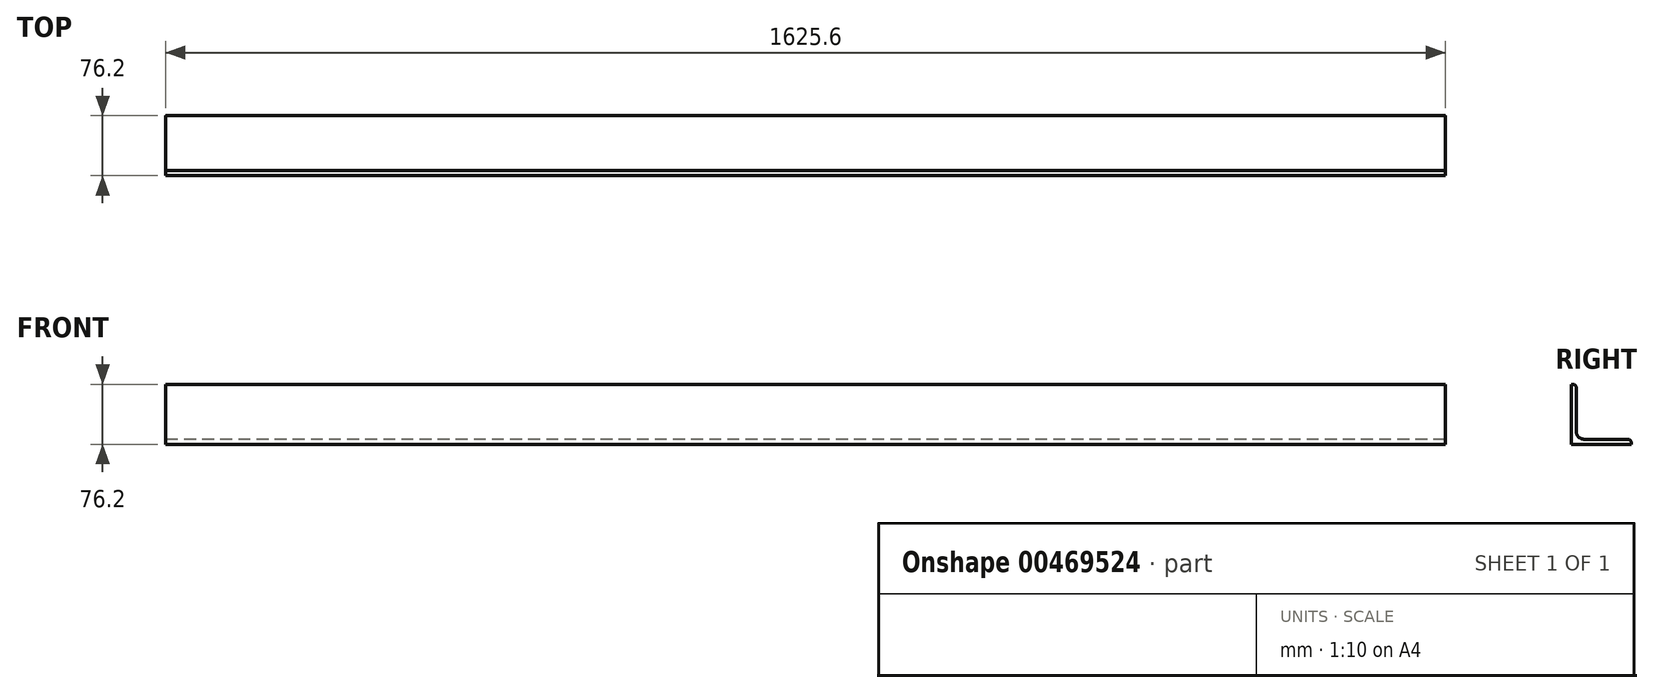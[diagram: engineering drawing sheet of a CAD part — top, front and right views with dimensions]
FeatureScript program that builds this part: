
annotation { "Feature Type Name" : "Feature", "Feature Type Description" : "" }
export const myFeature = defineFeature(function(context is Context, id is Id, definition is map)
    precondition{}
    {
        {
            var Q0;
            Q0=qCreatedBy(makeId("Right.planeOp"),FACE);
            var sketch = newSketch(context, id + "F0", { "sketchPlane" : qUnion([Q0])});
            skLineSegment(sketch, "E0", {"start": v(0, 76.2) * mm, "end": v(0, 0) * mm});
            skLineSegment(sketch, "E1", {"start": v(0, 0) * mm, "end": v(76.2, 0) * mm});
            skLineSegment(sketch, "E2", {"start": v(76.2, 0) * mm, "end": v(76.2, 1.59) * mm});
            skLineSegment(sketch, "E3", {"start": v(71.44, 6.35) * mm, "end": v(15.88, 6.35) * mm});
            skLineSegment(sketch, "E4", {"start": v(6.35, 15.87) * mm, "end": v(6.35, 71.44) * mm});
            skLineSegment(sketch, "E5", {"start": v(1.59, 76.2) * mm, "end": v(0, 76.2) * mm});
            skPoint(sketch, "E6.visualSharp", {"position": v(6.35, 76.2) * mm});
            skArc(sketch, "E6.filletArc", {"start": v(6.35, 71.44) * mm, "mid": v(4.96, 74.8) * mm, "end": v(1.59, 76.2) * mm});
            skPoint(sketch, "E7.visualSharp", {"position": v(76.2, 6.35) * mm});
            skArc(sketch, "E7.filletArc", {"start": v(76.2, 1.59) * mm, "mid": v(74.8, 4.96) * mm, "end": v(71.44, 6.35) * mm});
            skPoint(sketch, "E8.visualSharp", {"position": v(6.35, 6.35) * mm});
            skArc(sketch, "E8.filletArc", {"start": v(6.35, 15.87) * mm, "mid": v(9.14, 9.14) * mm, "end": v(15.88, 6.35) * mm});
            skSolve(sketch);
        }
        {
            var Q0;
            Q0=qSketchRegion(id+"F0",true);
            extrude(context, id + "F1", {"entities" : qUnion([Q0]), "endBound" : BoundingType.SYMMETRIC, "depth" : 1625.6 * mm});
        }
    });
